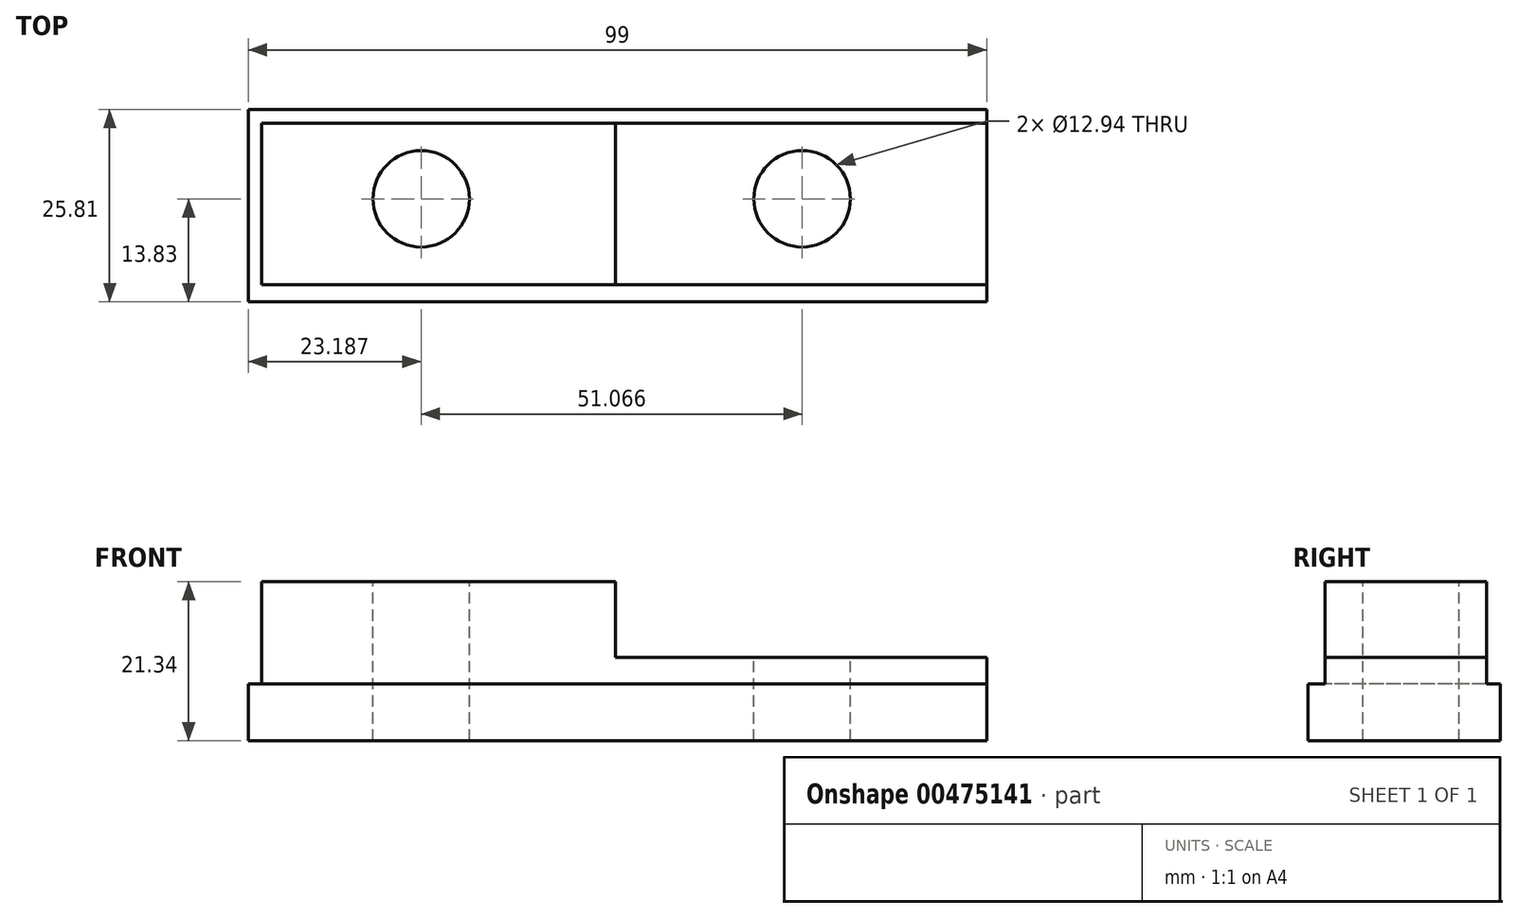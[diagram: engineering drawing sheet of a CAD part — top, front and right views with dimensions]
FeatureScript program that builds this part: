
annotation { "Feature Type Name" : "Feature", "Feature Type Description" : "" }
export const myFeature = defineFeature(function(context is Context, id is Id, definition is map)
    precondition{}
    {
        {
            var Q0;
            Q0=qCreatedBy(makeId("Top.planeOp"),FACE);
            var sketch = newSketch(context, id + "F0", { "sketchPlane" : qUnion([Q0])});
            skLineSegment(sketch, "E0.bottom", {"start": v(-49.22, 11.98) * mm, "end": v(49.78, 11.98) * mm});
            skLineSegment(sketch, "E0.top", {"start": v(-49.22, -13.83) * mm, "end": v(49.78, -13.83) * mm});
            skLineSegment(sketch, "E0.left", {"start": v(-49.22, 11.98) * mm, "end": v(-49.22, -13.83) * mm});
            skLineSegment(sketch, "E0.right", {"start": v(49.78, 11.98) * mm, "end": v(49.78, -13.83) * mm});
            skSolve(sketch);
        }
        {
            var Q0;
            Q0 = qSketchRegion(id + "F0", true);
            extrude(context, id + "F1", {"entities" : qUnion([Q0]), "depth" : 7.62 * mm});
        }
        {
            var Q0;
            Q0=makeQuery(id+"F1.opExtrude","CAP_FACE",FACE,{"disambiguationData":[OSD([sQuery(id+"F0.wireOp",EDGE,"E0.bottom"),sQuery(id+"F0.wireOp",EDGE,"E0.top"),sQuery(id+"F0.wireOp",EDGE,"E0.left"),sQuery(id+"F0.wireOp",EDGE,"E0.right")])],"isStart":false});
            var sketch = newSketch(context, id + "F2", { "sketchPlane" : qUnion([Q0])});
            skLineSegment(sketch, "E1.bottom", {"start": v(-47.42, 10.14) * mm, "end": v(49.78, 10.14) * mm});
            skLineSegment(sketch, "E1.top", {"start": v(-47.42, -11.52) * mm, "end": v(49.78, -11.52) * mm});
            skLineSegment(sketch, "E1.left", {"start": v(-47.42, 10.14) * mm, "end": v(-47.42, -11.52) * mm});
            skLineSegment(sketch, "E1.right", {"start": v(49.78, 10.14) * mm, "end": v(49.78, -11.52) * mm});
            skSolve(sketch);
        }
        {
            var Q0;
            Q0 = qSketchRegion(id + "F2", true);
            extrude(context, id + "F3", {"entities" : qUnion([Q0]), "operationType" : NewBodyOperationType.ADD, "depth" : 3.56 * mm});
        }
        {
            var Q0;
            Q0=makeQuery(id+"F3.opExtrude","CAP_FACE",FACE,{"disambiguationData":[OSD([sQuery(id+"F2.wireOp",EDGE,"E1.bottom"),sQuery(id+"F2.wireOp",EDGE,"E1.top"),sQuery(id+"F2.wireOp",EDGE,"E1.left"),sQuery(id+"F2.wireOp",EDGE,"E1.right")])],"isStart":false});
            var sketch = newSketch(context, id + "F4", { "sketchPlane" : qUnion([Q0])});
            skPoint(sketch, "E2.oppositeSnap0", {"position": v(1.18, -11.52) * mm});
            skLineSegment(sketch, "E2.bottom", {"start": v(-47.42, 10.14) * mm, "end": v(0, 10.14) * mm});
            skLineSegment(sketch, "E2.top", {"start": v(-47.42, -11.52) * mm, "end": v(0, -11.52) * mm});
            skLineSegment(sketch, "E2.left", {"start": v(-47.42, 10.14) * mm, "end": v(-47.42, -11.52) * mm});
            skLineSegment(sketch, "E2.right", {"start": v(0, 10.14) * mm, "end": v(0, -11.52) * mm});
            skSolve(sketch);
        }
        {
            var Q0;
            Q0 = qSketchRegion(id + "F4", true);
            extrude(context, id + "F5", {"entities" : qUnion([Q0]), "operationType" : NewBodyOperationType.ADD, "depth" : 10.16 * mm});
        }
        {
            var Q0;
            Q0=makeQuery(id+"F5.opExtrude","CAP_FACE",FACE,{"disambiguationData":[OSD([sQuery(id+"F4.wireOp",EDGE,"E2.bottom"),sQuery(id+"F4.wireOp",EDGE,"E2.top"),sQuery(id+"F4.wireOp",EDGE,"E2.left"),sQuery(id+"F4.wireOp",EDGE,"E2.right")])],"isStart":false});
            var sketch = newSketch(context, id + "F6", { "sketchPlane" : qUnion([Q0])});
            skCircle(sketch, "E3", {"center": v(-26.03, 0) * mm, "radius": 6.47 * mm});
            skCircle(sketch, "E4", {"center": v(25.03, 0) * mm, "radius": 6.47 * mm});
            skSolve(sketch);
        }
        {
            var Q0;
            Q0 = qSketchRegion(id + "F6", true);
            extrude(context, id + "F7", {"entities" : qUnion([Q0]), "operationType" : NewBodyOperationType.REMOVE, "oppositeDirection" : true, "depth" : 21.84 * mm});
        }
    });
